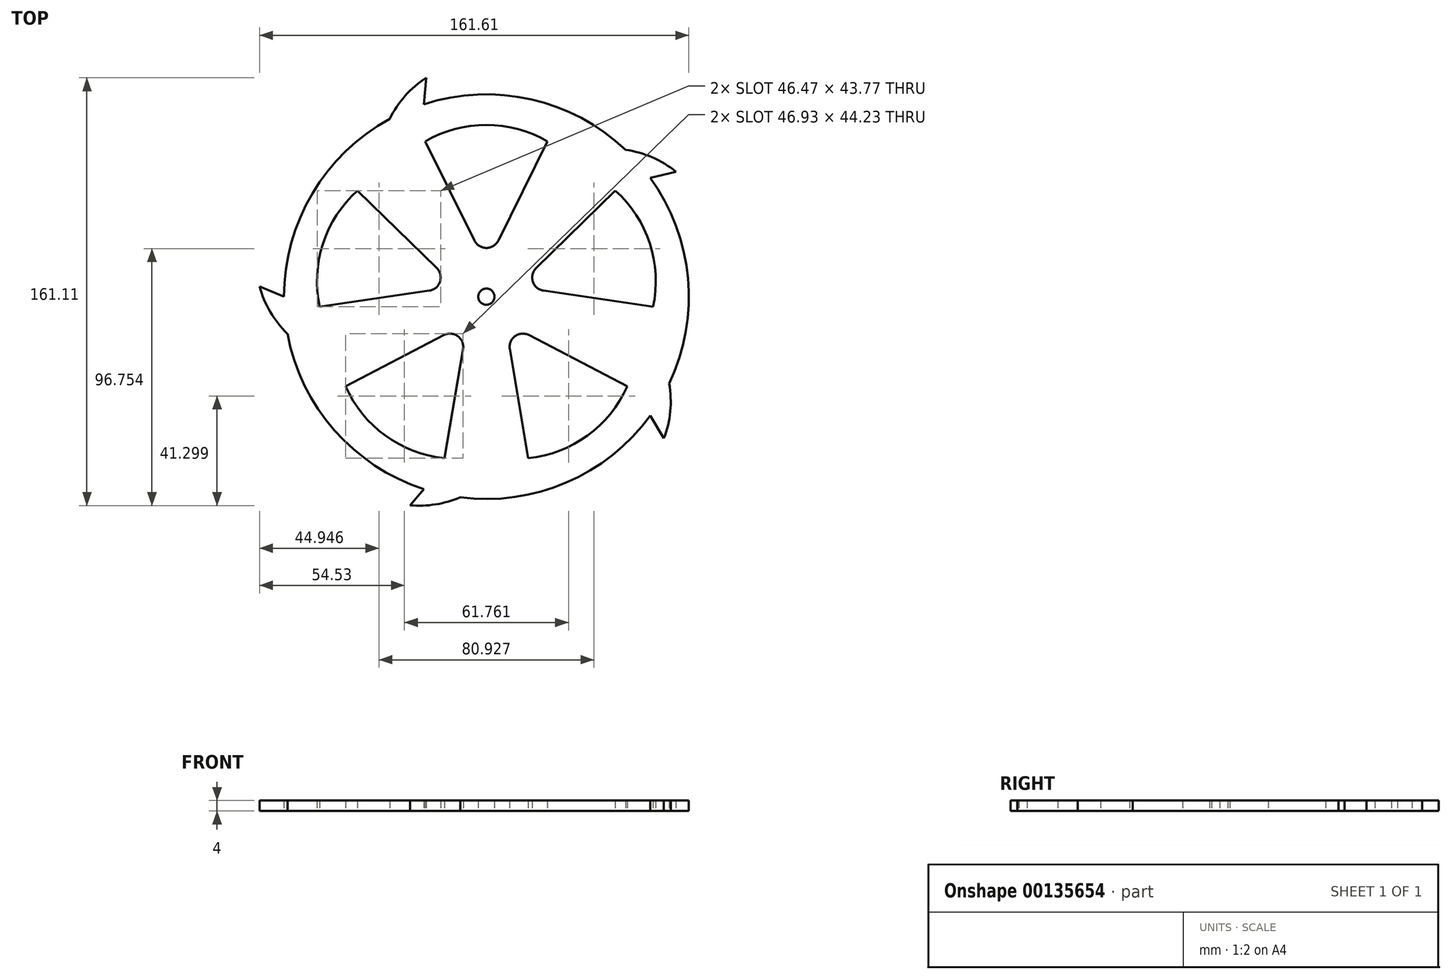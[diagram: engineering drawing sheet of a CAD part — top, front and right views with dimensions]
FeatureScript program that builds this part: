
annotation { "Feature Type Name" : "Feature", "Feature Type Description" : "" }
export const myFeature = defineFeature(function(context is Context, id is Id, definition is map)
    precondition{}
    {
        {
            var Q0;
            Q0=qCreatedBy(makeId("Top.planeOp"),FACE);
            var sketch = newSketch(context, id + "F0", { "sketchPlane" : qUnion([Q0])});
            skArc(sketch, "E0", {"start": v(-74.91, -13.95) * mm, "mid": v(-57.27, -50.27) * mm, "end": v(-23.55, -72.47) * mm});
            skLineSegment(sketch, "E1", {"start": v(-76.2, 0) * mm, "end": v(-85.41, 3.89) * mm});
            skArc(sketch, "E2", {"start": v(-85.41, 3.89) * mm, "mid": v(-81.37, -5.74) * mm, "end": v(-74.91, -13.95) * mm});
            skLineSegment(sketch, "E3.1.0", {"start": v(-23.55, -72.47) * mm, "end": v(-28.78, -78.52) * mm});
            skArc(sketch, "E3.1.1", {"start": v(-28.78, -78.52) * mm, "mid": v(-19.15, -78.21) * mm, "end": v(-9.88, -75.56) * mm});
            skLineSegment(sketch, "E3.2.0", {"start": v(61.65, -44.79) * mm, "end": v(66.81, -53.35) * mm});
            skArc(sketch, "E3.2.1", {"start": v(66.81, -53.35) * mm, "mid": v(69.2, -43.18) * mm, "end": v(68.8, -32.74) * mm});
            skLineSegment(sketch, "E3.3.0", {"start": v(61.65, 44.79) * mm, "end": v(71.39, 47.06) * mm});
            skArc(sketch, "E3.3.1", {"start": v(71.39, 47.06) * mm, "mid": v(62.45, 52.47) * mm, "end": v(52.4, 55.32) * mm});
            skLineSegment(sketch, "E3.4.0", {"start": v(-23.55, 72.47) * mm, "end": v(-22.7, 82.43) * mm});
            skArc(sketch, "E3.4.1", {"start": v(-22.7, 82.43) * mm, "mid": v(-30.6, 75.61) * mm, "end": v(-36.42, 66.93) * mm});
            skArc(sketch, "E4.trimOffspring", {"start": v(-36.42, 66.93) * mm, "mid": v(-65.5, 38.93) * mm, "end": v(-76.2, 0) * mm});
            skArc(sketch, "E5.trimOffspring", {"start": v(52.4, 55.32) * mm, "mid": v(16.78, 74.33) * mm, "end": v(-23.55, 72.47) * mm});
            skArc(sketch, "E6.trimOffspring", {"start": v(68.8, -32.74) * mm, "mid": v(75.88, 7) * mm, "end": v(61.65, 44.79) * mm});
            skArc(sketch, "E7.trimOffspring", {"start": v(-9.88, -75.56) * mm, "mid": v(30.11, -70) * mm, "end": v(61.65, -44.79) * mm});
            skCircle(sketch, "E8", {"center": v(0, 0) * mm, "radius": 3.05 * mm});
            skLineSegment(sketch, "E9", {"start": v(4.48, 21.14) * mm, "end": v(23.01, 58.49) * mm});
            skLineSegment(sketch, "E10.MirrorCS", {"start": v(-4.48, 21.14) * mm, "end": v(-23.01, 58.49) * mm});
            skArc(sketch, "E11", {"start": v(23.01, 58.49) * mm, "mid": v(0, 64.68) * mm, "end": v(-23.01, 58.49) * mm});
            skPoint(sketch, "E12.visualSharp", {"position": v(0, 12.12) * mm});
            skArc(sketch, "E12.filletArc", {"start": v(-4.48, 21.14) * mm, "mid": v(0, 18.37) * mm, "end": v(4.48, 21.14) * mm});
            skPoint(sketch, "E13.1.0", {"position": v(-11.53, 3.75) * mm});
            skArc(sketch, "E13.1.1", {"start": v(-48.52, 39.96) * mm, "mid": v(-61.52, 19.99) * mm, "end": v(-62.74, -3.81) * mm});
            skLineSegment(sketch, "E13.1.2", {"start": v(-21.5, 2.27) * mm, "end": v(-62.74, -3.81) * mm});
            skArc(sketch, "E13.1.3", {"start": v(-21.5, 2.27) * mm, "mid": v(-17.47, 5.68) * mm, "end": v(-18.73, 10.8) * mm});
            skLineSegment(sketch, "E13.1.4", {"start": v(-18.73, 10.8) * mm, "end": v(-48.52, 39.96) * mm});
            skPoint(sketch, "E13.2.0", {"position": v(-7.12, -9.8) * mm});
            skArc(sketch, "E13.2.1", {"start": v(-53, -33.8) * mm, "mid": v(-38.02, -52.33) * mm, "end": v(-15.76, -60.84) * mm});
            skLineSegment(sketch, "E13.2.2", {"start": v(-8.8, -19.74) * mm, "end": v(-15.76, -60.84) * mm});
            skArc(sketch, "E13.2.3", {"start": v(-8.8, -19.74) * mm, "mid": v(-10.8, -14.86) * mm, "end": v(-16.05, -14.47) * mm});
            skLineSegment(sketch, "E13.2.4", {"start": v(-16.05, -14.47) * mm, "end": v(-53, -33.8) * mm});
            skPoint(sketch, "E13.3.0", {"position": v(7.12, -9.8) * mm});
            skArc(sketch, "E13.3.1", {"start": v(15.76, -60.84) * mm, "mid": v(38.02, -52.33) * mm, "end": v(53, -33.8) * mm});
            skLineSegment(sketch, "E13.3.2", {"start": v(16.05, -14.47) * mm, "end": v(53, -33.8) * mm});
            skArc(sketch, "E13.3.3", {"start": v(16.05, -14.47) * mm, "mid": v(10.8, -14.86) * mm, "end": v(8.8, -19.74) * mm});
            skLineSegment(sketch, "E13.3.4", {"start": v(8.8, -19.74) * mm, "end": v(15.76, -60.84) * mm});
            skPoint(sketch, "E13.4.0", {"position": v(11.53, 3.75) * mm});
            skArc(sketch, "E13.4.1", {"start": v(62.74, -3.81) * mm, "mid": v(61.52, 19.99) * mm, "end": v(48.52, 39.96) * mm});
            skLineSegment(sketch, "E13.4.2", {"start": v(18.73, 10.8) * mm, "end": v(48.52, 39.96) * mm});
            skArc(sketch, "E13.4.3", {"start": v(18.73, 10.8) * mm, "mid": v(17.47, 5.68) * mm, "end": v(21.5, 2.27) * mm});
            skLineSegment(sketch, "E13.4.4", {"start": v(21.5, 2.27) * mm, "end": v(62.74, -3.81) * mm});
            skSolve(sketch);
        }
        {
            var Q0;
            Q0=makeQuery(id+"F0.imprint","IMPRINT",FACE,{"disambiguationData":[TD([[makeQuery(id+"F0.imprint","IMPRINT",EDGE,{"derivedFrom":sQuery(id+"F0.wireOp",EDGE,"E0")}),1.0]])]});
            extrude(context, id + "F1", {"entities" : qUnion([Q0]), "depth" : 4 * mm});
        }
    });
